# Revit family: NAU_Naughtone_Tbls_Tier_Metric_AFTERQA
name_source: partatom
category: Furniture
units: mm (PartAtom-declared; Revit-internal decimal feet)

## family parameters
Always vertical = Yes
Cut with Voids When Loaded = No
OmniClass Number = 23.40.20.00
OmniClass Title = General Furniture and Specialties
Room Calculation Point = No
Shared = No
Work Plane-Based = No

## types (13) — shared parameters
Assembly Code = E2020200
AssetType = Movable
BIMObjectName = NAU_Naughtone_Tables_Tier
Category = Pr_40_50_21 : Desks, tables and worktops
Color = Black base. White MFMDF top
DurationUnit = year
Features = Base plate and stem can come in different RAL finishes. See Tier - Options Breakdown document
Finish = Base is powdercoated steel in RAL 9005 black
IfcExportAs = IfcFurnishingElementType
IfcExportType = TABLE
ManufacturerAddress = Knaresborough Tech Park, Manse Lane, Knaresborough, HG5 8LF
ManufacturerName = Naughtone
ManufacturerURL = www.naughtone.com
Material = Base in steel. Top in MFMDF, veneered MDF, or Forbo bonded to MDF
NBSDescription = Tables
NBSReference = 45-35-86/327
Name = Tables_Tier_Naughtone
ProductInformation = https://www.naughtone.com
URL = www.naughtone.com
Uniclass2015Code = Pr_40_50_21
Uniclass2015Title = Desks, tables and worktops
Uniclass2015Version = Products v1.26
Version = 1
WarrantyDescription = Request warranty information from naughtone
WarrantyDurationLabor = 10
WarrantyDurationParts = 10
WarrantyDurationUnit = year
zero-valued in all types: Default Elevation, WorksurfaceArea

## per-type parameters (varying)
| type | BaseRadius | IsCircularTableTop | IsSquareTableTop | LegRadius | ModelNumber | NominalHeight | NominalLength | NominalWidth | Radius | Shape | Size | UndersidePlate | a |
| Tier 600 Circular Café Table | 225 mm  [stored 0.738189 ft] | Yes | No | 25 mm  [stored 0.082021 ft] | NOTIE3600D | 740 mm | 600 mm | 600 mm | 300 mm | Circular | 600 x 600 x 740mm | 250 mm  [stored 0.82021 ft] | 207 mm  [stored 0.679134 ft] |
| Tier 750 Circular Café Table | 275 mm | Yes | No | 40 mm  [stored 0.131234 ft] | NOTIE3750D | 740 mm | 750 mm  [stored 2.46063 ft] | 750 mm  [stored 2.46063 ft] | 375 mm  [stored 1.23031 ft] | Circular | 750 x 750 x 740mm | 250 mm  [stored 0.82021 ft] | 257 mm  [stored 0.843176 ft] |
| Tier 900 Circular Café Table | 275 mm | Yes | No | 40 mm  [stored 0.131234 ft] | NOTIE3900D | 740 mm | 900 mm  [stored 2.95276 ft] | 900 mm  [stored 2.95276 ft] | 450 mm  [stored 1.47638 ft] | Circular | 900 x 900 x 740mm | 250 mm  [stored 0.82021 ft] | 257 mm  [stored 0.843176 ft] |
| Tier 1050 Circular Café Table | 325 mm  [stored 1.06627 ft] | Yes | No | 50 mm  [stored 0.164042 ft] | NOTIE31050D | 740 mm | 1050 mm | 1050 mm | 525 mm  [stored 1.72244 ft] | Circular | 1050 x 1050 x 740mm | 400 mm  [stored 1.31234 ft] | 307 mm  [stored 1.00722 ft] |
| Tier 1200 Circular Café Table | 325 mm  [stored 1.06627 ft] | Yes | No | 50 mm  [stored 0.164042 ft] | NOTIE31200D | 740 mm | 1200 mm | 1200 mm | 600 mm | Circular | 1200 x 1200 x 740mm | 400 mm  [stored 1.31234 ft] | 307 mm  [stored 1.00722 ft] |
| Tier 600 Square Café Table | 225 mm  [stored 0.738189 ft] | No | Yes | 25 mm  [stored 0.082021 ft] | NOTIE3600S | 740 mm | 600 mm | 600 mm | 300 mm | Square | 600 x 600 x 740mm | 250 mm  [stored 0.82021 ft] | 207 mm  [stored 0.679134 ft] |
| Tier 750 Square Café Table | 275 mm | No | Yes | 40 mm  [stored 0.131234 ft] | NOTIE3750S | 740 mm | 750 mm  [stored 2.46063 ft] | 750 mm  [stored 2.46063 ft] | 375 mm  [stored 1.23031 ft] | Square | 750 x 750 x 740mm | 250 mm  [stored 0.82021 ft] | 257 mm  [stored 0.843176 ft] |
| Tier 900 Square Café Table | 275 mm | No | Yes | 40 mm  [stored 0.131234 ft] | NOTIE3900S | 740 mm | 900 mm  [stored 2.95276 ft] | 900 mm  [stored 2.95276 ft] | 450 mm  [stored 1.47638 ft] | Square | 900 x 900 x 740mm | 250 mm  [stored 0.82021 ft] | 257 mm  [stored 0.843176 ft] |
| Tier 1050 Square Café Table | 325 mm  [stored 1.06627 ft] | No | Yes | 50 mm  [stored 0.164042 ft] | NOTIE31050S | 740 mm | 1050 mm | 1050 mm | 525 mm  [stored 1.72244 ft] | Square | 1050 x 1050 x 740mm | 400 mm  [stored 1.31234 ft] | 307 mm  [stored 1.00722 ft] |
| Tier 1200 Square Café Table | 325 mm  [stored 1.06627 ft] | No | Yes | 50 mm  [stored 0.164042 ft] | NOTIE31200S | 740 mm | 1200 mm | 1200 mm | 600 mm | Square | 1200 x 1200 x 740mm | 400 mm  [stored 1.31234 ft] | 307 mm  [stored 1.00722 ft] |
| Tier 600 Circular Bar Height Table | 225 mm  [stored 0.738189 ft] | Yes | No | 25 mm  [stored 0.082021 ft] | NOTIE5600D | 1050 mm | 600 mm | 600 mm | 300 mm | Circular | 600 x 600 x 1050mm | 250 mm  [stored 0.82021 ft] | 207 mm  [stored 0.679134 ft] |
| Tier 600 Square Bar Height Table | 225 mm  [stored 0.738189 ft] | No | Yes | 25 mm  [stored 0.082021 ft] | NOTIE5600S | 1050 mm | 600 mm | 600 mm | 300 mm | Square | 600 x 600 x 1050mm | 250 mm  [stored 0.82021 ft] | 207 mm  [stored 0.679134 ft] |
| Tier 1500 Circular Café Table | 325 mm  [stored 1.06627 ft] | Yes | No | 50 mm  [stored 0.164042 ft] | NOTIE31500D | 740 mm | 1500 mm  [stored 4.92126 ft] | 1500 mm  [stored 4.92126 ft] | 750 mm  [stored 2.46063 ft] | Circular | 1500 x 1500 x 740mm | 400 mm  [stored 1.31234 ft] | 307 mm  [stored 1.00722 ft] |

note: column(s) folded — value = type name in every type: ModelReference

note: [stored X ft] marks values corroborated as IEEE doubles in the binary element streams (Revit-internal decimal feet)

## geometry (parser evidence)
native form markers: Sweep x5
no freeform markers — native parametric forms only
